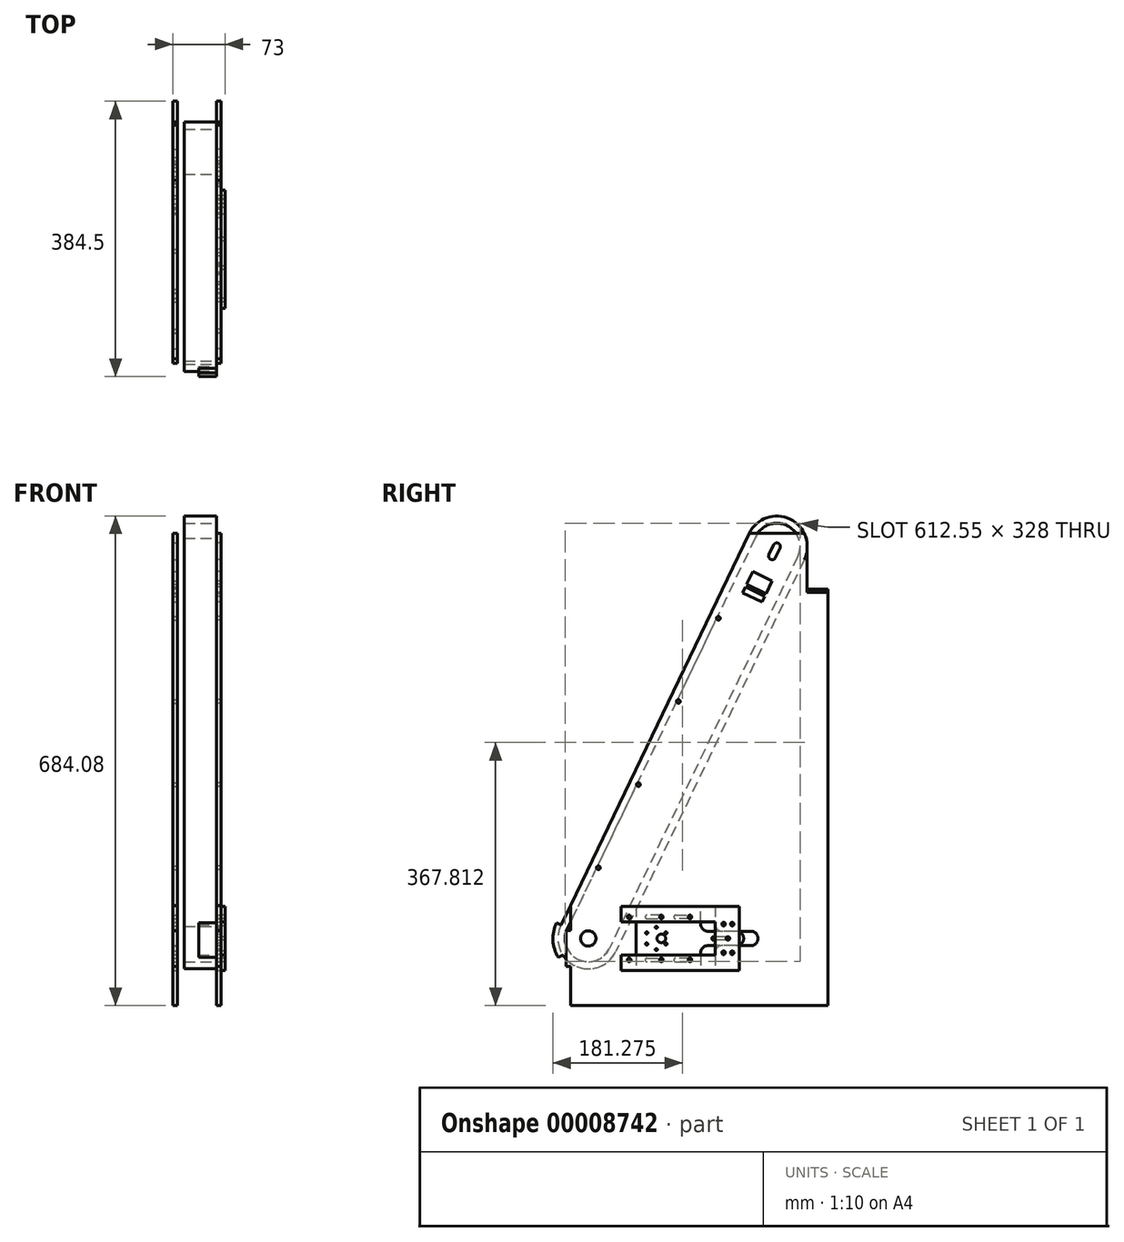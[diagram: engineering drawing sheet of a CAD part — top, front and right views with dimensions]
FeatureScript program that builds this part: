
annotation { "Feature Type Name" : "Feature", "Feature Type Description" : "" }
export const myFeature = defineFeature(function(context is Context, id is Id, definition is map)
    precondition{}
    {
        {
            var Q0;
            Q0=qCreatedBy(makeId("Right.planeOp"),FACE);
            var sketch = newSketch(context, id + "F0", { "sketchPlane" : qUnion([Q0])});
            skLineSegment(sketch, "E0", {"start": v(-250, 0) * mm, "end": v(-250, 45) * mm});
            skLineSegment(sketch, "E1", {"start": v(-250, 130) * mm, "end": v(0, 650) * mm});
            skLineSegment(sketch, "E2", {"start": v(0, 650) * mm, "end": v(0, 650) * mm});
            skLineSegment(sketch, "E3", {"start": v(0, 650) * mm, "end": v(0, 0) * mm, "construction": true});
            skLineSegment(sketch, "E4", {"start": v(0, 0) * mm, "end": v(-250, 0) * mm, "construction": true});
            skCircle(sketch, "E5", {"center": v(-225, 83.91) * mm, "radius": 32.5 * mm, "construction": true});
            skCircle(sketch, "E6", {"center": v(38.3, 631.58) * mm, "radius": 32.5 * mm, "construction": true});
            skLineSegment(sketch, "E7.bottom", {"start": v(-250, 0) * mm, "end": v(-400, 0) * mm, "construction": true});
            skLineSegment(sketch, "E7.top", {"start": v(-250, 130) * mm, "end": v(-400, 130) * mm, "construction": true});
            skLineSegment(sketch, "E7.left", {"start": v(-250, 0) * mm, "end": v(-250, 130) * mm, "construction": true});
            skLineSegment(sketch, "E7.right", {"start": v(-400, 0) * mm, "end": v(-400, 130) * mm, "construction": true});
            skLineSegment(sketch, "E8.bottom", {"start": v(0, 650) * mm, "end": v(150, 650) * mm, "construction": true});
            skLineSegment(sketch, "E8.top", {"start": v(0, 0) * mm, "end": v(150, 0) * mm, "construction": true});
            skLineSegment(sketch, "E8.right", {"start": v(150, 650) * mm, "end": v(150, 0) * mm, "construction": true});
            skLineSegment(sketch, "E9", {"start": v(110, 567.38) * mm, "end": v(110, 0) * mm});
            skCircle(sketch, "E10", {"center": v(38.3, 631.58) * mm, "radius": 42.5 * mm, "construction": true});
            skLineSegment(sketch, "E11", {"start": v(-215, 0) * mm, "end": v(-215, 122.02) * mm, "construction": true});
            skLineSegment(sketch, "E12", {"start": v(-215, 122.02) * mm, "end": v(-250, 130) * mm, "construction": true});
            skLineSegment(sketch, "E13", {"start": v(-215, 122.02) * mm, "end": v(-35, 496.42) * mm, "construction": true});
            skLineSegment(sketch, "E14", {"start": v(-35, 577.2) * mm, "end": v(-35, 0) * mm, "construction": true});
            skLineSegment(sketch, "E15.bottom", {"start": v(-250, 130) * mm, "end": v(-256, 130) * mm, "construction": true});
            skLineSegment(sketch, "E15.top", {"start": v(-250, 0) * mm, "end": v(-256, 0) * mm, "construction": true});
            skLineSegment(sketch, "E15.left", {"start": v(-250, 130) * mm, "end": v(-250, 0) * mm, "construction": true});
            skLineSegment(sketch, "E15.right", {"start": v(-256, 130) * mm, "end": v(-256, 0) * mm, "construction": true});
            skLineSegment(sketch, "E16.bottom", {"start": v(-256, 0) * mm, "end": v(-262, 0) * mm, "construction": true});
            skLineSegment(sketch, "E16.top", {"start": v(-256, 130) * mm, "end": v(-262, 130) * mm, "construction": true});
            skLineSegment(sketch, "E16.left", {"start": v(-256, 0) * mm, "end": v(-256, 130) * mm, "construction": true});
            skLineSegment(sketch, "E16.right", {"start": v(-262, 0) * mm, "end": v(-262, 130) * mm, "construction": true});
            skLineSegment(sketch, "E17.bottom", {"start": v(-215, 0) * mm, "end": v(-35, 0) * mm, "construction": true});
            skLineSegment(sketch, "E17.top", {"start": v(-215, 35) * mm, "end": v(-35, 35) * mm, "construction": true});
            skLineSegment(sketch, "E17.left", {"start": v(-215, 0) * mm, "end": v(-215, 35) * mm, "construction": true});
            skLineSegment(sketch, "E17.right", {"start": v(-35, 0) * mm, "end": v(-35, 35) * mm, "construction": true});
            skLineSegment(sketch, "E18.bottom", {"start": v(-215, 122.02) * mm, "end": v(-35, 122.02) * mm, "construction": true});
            skLineSegment(sketch, "E18.top", {"start": v(-215, 83.91) * mm, "end": v(-35, 83.91) * mm, "construction": true});
            skLineSegment(sketch, "E18.left", {"start": v(-215, 122.02) * mm, "end": v(-215, 83.91) * mm, "construction": true});
            skLineSegment(sketch, "E19", {"start": v(76.6, 650) * mm, "end": v(0, 650) * mm});
            skLineSegment(sketch, "E20", {"start": v(110, 0) * mm, "end": v(-35, 0) * mm, "construction": true});
            skArc(sketch, "E21", {"start": v(42.8, 629.42) * mm, "mid": v(40.47, 636.1) * mm, "end": v(33.8, 633.75) * mm});
            skLineSegment(sketch, "E22", {"start": v(33.8, 633.75) * mm, "end": v(27.3, 620.23) * mm});
            skLineSegment(sketch, "E23", {"start": v(42.8, 629.42) * mm, "end": v(36.31, 615.9) * mm});
            skArc(sketch, "E24.trimOffspring", {"start": v(27.3, 620.23) * mm, "mid": v(29.64, 613.56) * mm, "end": v(36.31, 615.9) * mm});
            skArc(sketch, "E25", {"start": v(80.8, 631.58) * mm, "mid": v(79.74, 641.03) * mm, "end": v(76.6, 650) * mm});
            skLineSegment(sketch, "E26", {"start": v(80.8, 631.58) * mm, "end": v(80.8, 567.38) * mm});
            skLineSegment(sketch, "E27", {"start": v(80.8, 567.38) * mm, "end": v(110, 567.38) * mm});
            skLineSegment(sketch, "E28.bottom", {"start": v(-5.55, 575) * mm, "end": v(21.5, 562) * mm});
            skLineSegment(sketch, "E28.top", {"start": v(-9.45, 566.89) * mm, "end": v(17.6, 553.89) * mm});
            skLineSegment(sketch, "E28.left", {"start": v(-5.55, 575) * mm, "end": v(-9.45, 566.89) * mm});
            skLineSegment(sketch, "E28.right", {"start": v(21.5, 562) * mm, "end": v(17.6, 553.89) * mm});
            skCircle(sketch, "E29", {"center": v(-43.2, 531.3) * mm, "radius": 2.5 * mm});
            skCircle(sketch, "E30", {"center": v(-154.93, 298.9) * mm, "radius": 2.5 * mm});
            skCircle(sketch, "E31", {"center": v(-210.8, 182.7) * mm, "radius": 2.5 * mm});
            skCircle(sketch, "E32", {"center": v(-99.06, 415.1) * mm, "radius": 2.5 * mm});
            skLineSegment(sketch, "E33", {"start": v(-43.2, 531.3) * mm, "end": v(-99.06, 415.1) * mm, "construction": true});
            skLineSegment(sketch, "E34", {"start": v(-99.06, 415.1) * mm, "end": v(-154.93, 298.9) * mm, "construction": true});
            skLineSegment(sketch, "E35", {"start": v(-154.93, 298.9) * mm, "end": v(-210.8, 182.7) * mm, "construction": true});
            skLineSegment(sketch, "E36.trimOffspring", {"start": v(-250, 95) * mm, "end": v(-250, 130) * mm});
            skLineSegment(sketch, "E37", {"start": v(-250, 45) * mm, "end": v(-256, 45) * mm});
            skLineSegment(sketch, "E38", {"start": v(-256, 45) * mm, "end": v(-256, 95) * mm});
            skLineSegment(sketch, "E39", {"start": v(-250, 95) * mm, "end": v(-256, 95) * mm});
            skCircle(sketch, "E40", {"center": v(-225, 83.91) * mm, "radius": 42.5 * mm, "construction": true});
            skCircle(sketch, "E41", {"center": v(-225, 83.91) * mm, "radius": 10.75 * mm});
            skLineSegment(sketch, "E42", {"start": v(38.3, 631.58) * mm, "end": v(-225, 83.91) * mm, "construction": true});
            skLineSegment(sketch, "E43", {"start": v(7.97, 568.5) * mm, "end": v(4.07, 560.39) * mm, "construction": true});
            skArc(sketch, "E44", {"start": v(-103, 77.41) * mm, "mid": v(-96.5, 83.91) * mm, "end": v(-103, 90.41) * mm, "construction": true});
            skArc(sketch, "E45", {"start": v(-123, 90.41) * mm, "mid": v(-129.5, 83.91) * mm, "end": v(-123, 77.41) * mm, "construction": true});
            skLineSegment(sketch, "E46", {"start": v(-123, 90.41) * mm, "end": v(-103, 90.41) * mm, "construction": true});
            skLineSegment(sketch, "E47", {"start": v(-103, 77.41) * mm, "end": v(-123, 77.41) * mm, "construction": true});
            skArc(sketch, "E48", {"start": v(-143, 116.41) * mm, "mid": v(-145.5, 113.91) * mm, "end": v(-143, 111.41) * mm, "construction": true});
            skArc(sketch, "E49", {"start": v(-123, 111.41) * mm, "mid": v(-120.5, 113.91) * mm, "end": v(-123, 116.41) * mm, "construction": true});
            skLineSegment(sketch, "E50", {"start": v(-123, 116.41) * mm, "end": v(-143, 116.41) * mm, "construction": true});
            skLineSegment(sketch, "E51", {"start": v(-143, 111.41) * mm, "end": v(-123, 111.41) * mm, "construction": true});
            skLineSegment(sketch, "E52", {"start": v(-113, 90.41) * mm, "end": v(-113, 77.41) * mm, "construction": true});
            skLineSegment(sketch, "E53.0.MirrorCS", {"start": v(-83, 111.41) * mm, "end": v(-103, 111.41) * mm, "construction": true});
            skArc(sketch, "E54.0.MirrorCS", {"start": v(-103, 111.41) * mm, "mid": v(-105.5, 113.91) * mm, "end": v(-103, 116.41) * mm, "construction": true});
            skLineSegment(sketch, "E55.0.MirrorCS", {"start": v(-103, 116.41) * mm, "end": v(-83, 116.41) * mm, "construction": true});
            skArc(sketch, "E56.0.MirrorCS", {"start": v(-83, 116.41) * mm, "mid": v(-80.5, 113.91) * mm, "end": v(-83, 111.41) * mm, "construction": true});
            skLineSegment(sketch, "E57.0.MirrorCS", {"start": v(-123, 51.41) * mm, "end": v(-143, 51.41) * mm, "construction": true});
            skArc(sketch, "E58.0.MirrorCS", {"start": v(-143, 51.41) * mm, "mid": v(-145.5, 53.91) * mm, "end": v(-143, 56.41) * mm, "construction": true});
            skLineSegment(sketch, "E59.0.MirrorCS", {"start": v(-103, 51.41) * mm, "end": v(-83, 51.41) * mm, "construction": true});
            skArc(sketch, "E60.0.MirrorCS", {"start": v(-123, 56.41) * mm, "mid": v(-120.5, 53.91) * mm, "end": v(-123, 51.41) * mm, "construction": true});
            skLineSegment(sketch, "E61.0.MirrorCS", {"start": v(-143, 56.41) * mm, "end": v(-123, 56.41) * mm, "construction": true});
            skArc(sketch, "E62.0.MirrorCS", {"start": v(-103, 56.41) * mm, "mid": v(-105.5, 53.91) * mm, "end": v(-103, 51.41) * mm, "construction": true});
            skLineSegment(sketch, "E63.0.MirrorCS", {"start": v(-83, 56.41) * mm, "end": v(-103, 56.41) * mm, "construction": true});
            skArc(sketch, "E64.0.MirrorCS", {"start": v(-83, 51.41) * mm, "mid": v(-80.5, 53.91) * mm, "end": v(-83, 56.41) * mm, "construction": true});
            skLineSegment(sketch, "E65", {"start": v(-250, 0) * mm, "end": v(-250, -10) * mm});
            skLineSegment(sketch, "E66", {"start": v(-250, -10) * mm, "end": v(110, -10) * mm});
            skLineSegment(sketch, "E67", {"start": v(110, -10) * mm, "end": v(110, 0) * mm});
            skLineSegment(sketch, "E68.bottom", {"start": v(-158, 128.91) * mm, "end": v(-48, 128.91) * mm});
            skLineSegment(sketch, "E68.top", {"start": v(-158, 38.91) * mm, "end": v(-48, 38.91) * mm});
            skLineSegment(sketch, "E68.left", {"start": v(-158, 128.91) * mm, "end": v(-158, 38.91) * mm});
            skLineSegment(sketch, "E68.right", {"start": v(-48, 128.91) * mm, "end": v(-48, 103.91) * mm});
            skLineSegment(sketch, "E69", {"start": v(2, 93.91) * mm, "end": v(-38, 93.91) * mm});
            skLineSegment(sketch, "E70", {"start": v(2, 73.91) * mm, "end": v(-38, 73.91) * mm});
            skLineSegment(sketch, "E71.trimOffspring", {"start": v(-48, 63.91) * mm, "end": v(-48, 38.91) * mm});
            skCircle(sketch, "E72", {"center": v(-36, 103.91) * mm, "radius": 2.5 * mm});
            skCircle(sketch, "E73", {"center": v(-24, 103.91) * mm, "radius": 2.5 * mm});
            skCircle(sketch, "E74.0.MirrorC", {"center": v(-36, 63.91) * mm, "radius": 2.5 * mm});
            skCircle(sketch, "E75.0.MirrorC", {"center": v(-24, 63.91) * mm, "radius": 2.5 * mm});
            skPoint(sketch, "E76.visualSharp", {"position": v(-48, 93.91) * mm});
            skArc(sketch, "E76.filletArc", {"start": v(-48, 103.91) * mm, "mid": v(-45.07, 96.84) * mm, "end": v(-38, 93.91) * mm});
            skPoint(sketch, "E77.visualSharp", {"position": v(-48, 73.91) * mm});
            skArc(sketch, "E77.filletArc", {"start": v(-38, 73.91) * mm, "mid": v(-45.07, 70.99) * mm, "end": v(-48, 63.91) * mm});
            skArc(sketch, "E78", {"start": v(2, 73.91) * mm, "mid": v(12, 83.91) * mm, "end": v(2, 93.91) * mm});
            skCircle(sketch, "E79", {"center": v(-168, 113.91) * mm, "radius": 2.5 * mm});
            skCircle(sketch, "E80", {"center": v(-168, 53.91) * mm, "radius": 2.5 * mm});
            skLineSegment(sketch, "E81", {"start": v(23.22, 565.6) * mm, "end": v(-3.81, 578.6) * mm});
            skLineSegment(sketch, "E82", {"start": v(-3.81, 578.6) * mm, "end": v(4.85, 596.63) * mm});
            skLineSegment(sketch, "E83", {"start": v(4.85, 596.63) * mm, "end": v(31.9, 583.63) * mm});
            skLineSegment(sketch, "E84", {"start": v(31.9, 583.63) * mm, "end": v(23.22, 565.6) * mm});
            skSolve(sketch);
        }
        {
            var Q0;
            Q0 = qSketchRegion(id + "F0", true);
            extrude(context, id + "F1", {"entities" : qUnion([Q0]), "depth" : 6 * mm});
        }
        {
            var Q0;
            Q0=makeQuery(id+"F0.imprint","IMPRINT",FACE,{"disambiguationData":[TD([[makeQuery(id+"F0.imprint","IMPRINT",EDGE,{"derivedFrom":sQuery(id+"F0.wireOp",EDGE,"E0")}),-1.0]])]});
            var sketch = newSketch(context, id + "F2", { "sketchPlane" : qUnion([Q0])});
            skArc(sketch, "E85.0", {"start": v(-263.3, 102.33) * mm, "mid": v(-243.42, 45.61) * mm, "end": v(-186.7, 65.5) * mm});
            skLineSegment(sketch, "E85.1", {"start": v(76.63, 613.22) * mm, "end": v(-186.7, 65.5) * mm});
            skLineSegment(sketch, "E85.2", {"start": v(67.61, 617.55) * mm, "end": v(-195.7, 69.83) * mm});
            skArc(sketch, "E85.3", {"start": v(-252.97, 100.46) * mm, "mid": v(-240.33, 55.26) * mm, "end": v(-195.7, 69.83) * mm});
            skLineSegment(sketch, "E85.4", {"start": v(-250, 130) * mm, "end": v(0, 650) * mm});
            skArc(sketch, "E85.5", {"start": v(76.63, 613.22) * mm, "mid": v(56.7, 669.9) * mm, "end": v(0, 650) * mm});
            skArc(sketch, "E85.6", {"start": v(67.61, 617.55) * mm, "mid": v(51.09, 661.46) * mm, "end": v(7.9, 643.1) * mm});
            skLineSegment(sketch, "E86", {"start": v(7.9, 643.1) * mm, "end": v(-252.97, 100.46) * mm});
            skLineSegment(sketch, "E87", {"start": v(-250, 130) * mm, "end": v(-263.3, 102.33) * mm});
            skSolve(sketch);
        }
        {
            var Q0;
            Q0 = qSketchRegion(id + "F2", true);
            extrude(context, id + "F3", {"entities" : qUnion([Q0]), "oppositeDirection" : true, "depth" : 45 * mm});
        }
        {
            var Q0;
            Q0=makeQuery(id+"F3.opExtrude","CAP_FACE",FACE,{"disambiguationData":[OSD([sQuery(id+"F2.wireOp",EDGE,"E85.0"),sQuery(id+"F2.wireOp",EDGE,"E85.1"),sQuery(id+"F2.wireOp",EDGE,"E85.2"),sQuery(id+"F2.wireOp",EDGE,"E85.3"),sQuery(id+"F2.wireOp",EDGE,"E85.4"),sQuery(id+"F2.wireOp",EDGE,"E85.5"),sQuery(id+"F2.wireOp",EDGE,"E85.6"),sQuery(id+"F2.wireOp",EDGE,"E86"),sQuery(id+"F2.wireOp",EDGE,"E87")])],"isStart":true});
            var sketch = newSketch(context, id + "F4", { "sketchPlane" : qUnion([Q0])});
            skArc(sketch, "E88", {"start": v(-269.4, 105.8) * mm, "mid": v(-274.43, 81.35) * mm, "end": v(-266.9, 57.55) * mm});
            skLineSegment(sketch, "E89", {"start": v(-269.4, 105.8) * mm, "end": v(-263.3, 102.33) * mm});
            skLineSegment(sketch, "E90", {"start": v(-266.9, 57.55) * mm, "end": v(-260.81, 61.03) * mm});
            skArc(sketch, "E91", {"start": v(-263.3, 102.33) * mm, "mid": v(-267.42, 81.36) * mm, "end": v(-260.81, 61.03) * mm});
            skSolve(sketch);
        }
        {
            var Q0;
            Q0 = qSketchRegion(id + "F4", true);
            extrude(context, id + "F5", {"entities" : qUnion([Q0]), "operationType" : NewBodyOperationType.ADD, "oppositeDirection" : true, "depth" : 25 * mm});
        }
        {
            var Q0;
            Q0=makeQuery(id+"F1.opExtrude","CAP_FACE",FACE,{"disambiguationData":[OSD([sQuery(id+"F0.wireOp",EDGE,"E0"),sQuery(id+"F0.wireOp",EDGE,"E1"),sQuery(id+"F0.wireOp",EDGE,"E9"),sQuery(id+"F0.wireOp",EDGE,"E19"),sQuery(id+"F0.wireOp",EDGE,"E21"),sQuery(id+"F0.wireOp",EDGE,"E22"),sQuery(id+"F0.wireOp",EDGE,"E23"),sQuery(id+"F0.wireOp",EDGE,"E24.trimOffspring"),sQuery(id+"F0.wireOp",EDGE,"E25"),sQuery(id+"F0.wireOp",EDGE,"E26"),sQuery(id+"F0.wireOp",EDGE,"E27"),sQuery(id+"F0.wireOp",EDGE,"E28.bottom"),sQuery(id+"F0.wireOp",EDGE,"E28.top"),sQuery(id+"F0.wireOp",EDGE,"E28.left"),sQuery(id+"F0.wireOp",EDGE,"E28.right"),sQuery(id+"F0.wireOp",EDGE,"E29"),sQuery(id+"F0.wireOp",EDGE,"E30"),sQuery(id+"F0.wireOp",EDGE,"E31"),sQuery(id+"F0.wireOp",EDGE,"E32"),sQuery(id+"F0.wireOp",EDGE,"E36.trimOffspring"),sQuery(id+"F0.wireOp",EDGE,"E37"),sQuery(id+"F0.wireOp",EDGE,"E38"),sQuery(id+"F0.wireOp",EDGE,"E39"),sQuery(id+"F0.wireOp",EDGE,"E41"),sQuery(id+"F0.wireOp",EDGE,"E65"),sQuery(id+"F0.wireOp",EDGE,"E66"),sQuery(id+"F0.wireOp",EDGE,"E67"),sQuery(id+"F0.wireOp",EDGE,"E68.bottom"),sQuery(id+"F0.wireOp",EDGE,"E68.top"),sQuery(id+"F0.wireOp",EDGE,"E68.left"),sQuery(id+"F0.wireOp",EDGE,"E68.right"),sQuery(id+"F0.wireOp",EDGE,"E69"),sQuery(id+"F0.wireOp",EDGE,"E70"),sQuery(id+"F0.wireOp",EDGE,"E71.trimOffspring"),sQuery(id+"F0.wireOp",EDGE,"E72"),sQuery(id+"F0.wireOp",EDGE,"E73"),sQuery(id+"F0.wireOp",EDGE,"E74.0.MirrorC"),sQuery(id+"F0.wireOp",EDGE,"E75.0.MirrorC"),sQuery(id+"F0.wireOp",EDGE,"E76.filletArc"),sQuery(id+"F0.wireOp",EDGE,"E77.filletArc"),sQuery(id+"F0.wireOp",EDGE,"E78"),sQuery(id+"F0.wireOp",EDGE,"5232d4b0-3cc3-4d14-9a51-cdb3d410511d.0.MirrorCS"),sQuery(id+"F0.wireOp",EDGE,"e2d33160-89aa-41c8-a270-ced146764406.0.MirrorCS"),sQuery(id+"F0.wireOp",EDGE,"e187159f-ad14-482b-9280-8cc7652cb730.0.MirrorCS"),sQuery(id+"F0.wireOp",EDGE,"d5b84b43-e90d-4140-bfef-c8227e2ab3ce.0.MirrorCS"),sQuery(id+"F0.wireOp",EDGE,"901432f0-0f95-4989-9cc0-a0deb5664f3d.0.MirrorCS"),sQuery(id+"F0.wireOp",EDGE,"20d51c83-01ba-4d90-888a-5c5246788dde.0.MirrorCS"),sQuery(id+"F0.wireOp",EDGE,"919df3ca-f2c8-442f-8c62-a2348701ab05.0.MirrorCS"),sQuery(id+"F0.wireOp",EDGE,"f4d91b0f-c379-4811-a7c1-4052a48fdef3.0.MirrorCS"),sQuery(id+"F0.wireOp",EDGE,"65e59967-7406-4aeb-97f1-becdd296b569.0.MirrorCS"),sQuery(id+"F0.wireOp",EDGE,"80b0b28f-4663-4f58-9bb3-9a96ce068a37.0.MirrorCS"),sQuery(id+"F0.wireOp",EDGE,"c9f270f5-1f51-4d0d-ae3f-d0e4d7b2f217.0.MirrorCS"),sQuery(id+"F0.wireOp",EDGE,"a8867294-c913-42ce-a77f-fa8c65982e2f.0.MirrorCS"),sQuery(id+"F0.wireOp",EDGE,"a8dd77a0-3a93-456d-83c1-19a94e0bbaab.0.MirrorCS"),sQuery(id+"F0.wireOp",EDGE,"77da776a-dfef-4cf4-8eb2-1489e33f5686.0.MirrorCS"),sQuery(id+"F0.wireOp",EDGE,"566fd665-dcc4-43ef-a258-170fd602a317.0.MirrorCS"),sQuery(id+"F0.wireOp",EDGE,"d3467c6b-eefe-44c7-bab6-9067eb3a1ad1.0.MirrorCS")])],"isStart":false});
            var sketch = newSketch(context, id + "F6", { "sketchPlane" : qUnion([Q0])});
            skLineSegment(sketch, "E92.bottom", {"start": v(-158, 128.91) * mm, "end": v(-68, 128.91) * mm});
            skLineSegment(sketch, "E92.top", {"start": v(-158, 38.91) * mm, "end": v(-68, 38.91) * mm});
            skLineSegment(sketch, "E92.left", {"start": v(-158, 128.91) * mm, "end": v(-158, 38.91) * mm});
            skCircle(sketch, "E93", {"center": v(-123, 83.91) * mm, "radius": 6 * mm});
            skArc(sketch, "E94", {"start": v(-18, 73.91) * mm, "mid": v(-8, 83.91) * mm, "end": v(-18, 93.91) * mm});
            skLineSegment(sketch, "E95", {"start": v(-18, 73.91) * mm, "end": v(-58, 73.91) * mm});
            skLineSegment(sketch, "E96", {"start": v(-68, 63.91) * mm, "end": v(-68, 38.91) * mm});
            skLineSegment(sketch, "E97", {"start": v(-18, 93.91) * mm, "end": v(-58, 93.91) * mm});
            skLineSegment(sketch, "E98", {"start": v(-68, 103.91) * mm, "end": v(-68, 128.91) * mm});
            skArc(sketch, "E99", {"start": v(-30, 81.41) * mm, "mid": v(-27.5, 83.91) * mm, "end": v(-30, 86.41) * mm});
            skLineSegment(sketch, "E100", {"start": v(-30, 86.41) * mm, "end": v(-50, 86.41) * mm});
            skLineSegment(sketch, "E101", {"start": v(-30, 81.41) * mm, "end": v(-50, 81.41) * mm});
            skArc(sketch, "E102", {"start": v(-50, 86.41) * mm, "mid": v(-52.5, 83.91) * mm, "end": v(-50, 81.41) * mm});
            skPoint(sketch, "E103.visualSharp", {"position": v(-68, 93.91) * mm});
            skArc(sketch, "E103.filletArc", {"start": v(-68, 103.91) * mm, "mid": v(-65.07, 96.84) * mm, "end": v(-58, 93.91) * mm});
            skPoint(sketch, "E104.visualSharp", {"position": v(-68, 73.91) * mm});
            skArc(sketch, "E104.filletArc", {"start": v(-58, 73.91) * mm, "mid": v(-65.07, 70.99) * mm, "end": v(-68, 63.91) * mm});
            skLineSegment(sketch, "E105", {"start": v(-8, 83.91) * mm, "end": v(12, 83.91) * mm, "construction": true});
            skLineSegment(sketch, "E106", {"start": v(-36, 103.91) * mm, "end": v(-24, 103.91) * mm, "construction": true});
            skLineSegment(sketch, "E107", {"start": v(-30, 103.91) * mm, "end": v(-30, 63.91) * mm, "construction": true});
            skLineSegment(sketch, "E108", {"start": v(-24, 63.91) * mm, "end": v(-36, 63.91) * mm, "construction": true});
            skCircle(sketch, "E109", {"center": v(-130, 83.91) * mm, "radius": 15.5 * mm, "construction": true});
            skCircle(sketch, "E110", {"center": v(-143.42, 91.66) * mm, "radius": 1.5 * mm});
            skCircle(sketch, "E111", {"center": v(-143.42, 76.16) * mm, "radius": 1.5 * mm});
            skCircle(sketch, "E112", {"center": v(-130, 68.41) * mm, "radius": 1.5 * mm});
            skCircle(sketch, "E113", {"center": v(-130, 99.41) * mm, "radius": 1.5 * mm});
            skCircle(sketch, "E114", {"center": v(-116.58, 91.66) * mm, "radius": 1.5 * mm});
            skLineSegment(sketch, "E115.2", {"start": v(-215, 83.91) * mm, "end": v(-35, 83.91) * mm});
            skLineSegment(sketch, "E116", {"start": v(-130, 83.91) * mm, "end": v(-130, 99.41) * mm, "construction": true});
            skLineSegment(sketch, "E117", {"start": v(-130, 83.91) * mm, "end": v(-143.42, 76.16) * mm, "construction": true});
            skLineSegment(sketch, "E118", {"start": v(-130, 83.91) * mm, "end": v(-116.58, 91.66) * mm, "construction": true});
            skLineSegment(sketch, "E119", {"start": v(-130, 83.91) * mm, "end": v(-130, 68.41) * mm, "construction": true});
            skCircle(sketch, "E120", {"center": v(-116.58, 76.16) * mm, "radius": 1.5 * mm});
            skLineSegment(sketch, "E121", {"start": v(-130, 83.91) * mm, "end": v(-143.42, 91.66) * mm, "construction": true});
            skLineSegment(sketch, "E122", {"start": v(-130, 83.91) * mm, "end": v(-116.58, 76.16) * mm, "construction": true});
            skLineSegment(sketch, "E123.0", {"start": v(-123, 116.41) * mm, "end": v(-143, 116.41) * mm});
            skArc(sketch, "E123.1", {"start": v(-123, 111.41) * mm, "mid": v(-120.5, 113.91) * mm, "end": v(-123, 116.41) * mm});
            skLineSegment(sketch, "E123.2", {"start": v(-103, 116.41) * mm, "end": v(-83, 116.41) * mm});
            skArc(sketch, "E123.3", {"start": v(-103, 111.41) * mm, "mid": v(-105.5, 113.91) * mm, "end": v(-103, 116.41) * mm});
            skLineSegment(sketch, "E123.4", {"start": v(-83, 111.41) * mm, "end": v(-103, 111.41) * mm});
            skArc(sketch, "E123.5", {"start": v(-83, 116.41) * mm, "mid": v(-80.5, 113.91) * mm, "end": v(-83, 111.41) * mm});
            skLineSegment(sketch, "E123.6", {"start": v(-143, 111.41) * mm, "end": v(-123, 111.41) * mm});
            skArc(sketch, "E123.7", {"start": v(-143, 116.41) * mm, "mid": v(-145.5, 113.91) * mm, "end": v(-143, 111.41) * mm});
            skLineSegment(sketch, "E123.8", {"start": v(-143, 56.41) * mm, "end": v(-123, 56.41) * mm});
            skArc(sketch, "E123.9", {"start": v(-143, 51.41) * mm, "mid": v(-145.5, 53.91) * mm, "end": v(-143, 56.41) * mm});
            skLineSegment(sketch, "E123.10", {"start": v(-123, 51.41) * mm, "end": v(-143, 51.41) * mm});
            skArc(sketch, "E123.11", {"start": v(-123, 56.41) * mm, "mid": v(-120.5, 53.91) * mm, "end": v(-123, 51.41) * mm});
            skLineSegment(sketch, "E123.12", {"start": v(-83, 56.41) * mm, "end": v(-103, 56.41) * mm});
            skArc(sketch, "E123.13", {"start": v(-103, 56.41) * mm, "mid": v(-105.5, 53.91) * mm, "end": v(-103, 51.41) * mm});
            skLineSegment(sketch, "E123.14", {"start": v(-103, 51.41) * mm, "end": v(-83, 51.41) * mm});
            skArc(sketch, "E123.15", {"start": v(-83, 51.41) * mm, "mid": v(-80.5, 53.91) * mm, "end": v(-83, 56.41) * mm});
            skSolve(sketch);
        }
        {
            var Q0;
            Q0 = qSketchRegion(id + "F6", true);
            extrude(context, id + "F7", {"entities" : qUnion([Q0]), "oppositeDirection" : true, "depth" : 6 * mm});
        }
        {
            var Q0;
            Q0=makeQuery(id+"F1.opExtrude","CAP_FACE",FACE,{"disambiguationData":[OSD([sQuery(id+"F0.wireOp",EDGE,"E0"),sQuery(id+"F0.wireOp",EDGE,"E1"),sQuery(id+"F0.wireOp",EDGE,"E9"),sQuery(id+"F0.wireOp",EDGE,"E19"),sQuery(id+"F0.wireOp",EDGE,"E21"),sQuery(id+"F0.wireOp",EDGE,"E22"),sQuery(id+"F0.wireOp",EDGE,"E23"),sQuery(id+"F0.wireOp",EDGE,"E24.trimOffspring"),sQuery(id+"F0.wireOp",EDGE,"E25"),sQuery(id+"F0.wireOp",EDGE,"E26"),sQuery(id+"F0.wireOp",EDGE,"E27"),sQuery(id+"F0.wireOp",EDGE,"E28.bottom"),sQuery(id+"F0.wireOp",EDGE,"E28.top"),sQuery(id+"F0.wireOp",EDGE,"E28.left"),sQuery(id+"F0.wireOp",EDGE,"E28.right"),sQuery(id+"F0.wireOp",EDGE,"E29"),sQuery(id+"F0.wireOp",EDGE,"E30"),sQuery(id+"F0.wireOp",EDGE,"E31"),sQuery(id+"F0.wireOp",EDGE,"E32"),sQuery(id+"F0.wireOp",EDGE,"E36.trimOffspring"),sQuery(id+"F0.wireOp",EDGE,"E37"),sQuery(id+"F0.wireOp",EDGE,"E38"),sQuery(id+"F0.wireOp",EDGE,"E39"),sQuery(id+"F0.wireOp",EDGE,"E41"),sQuery(id+"F0.wireOp",EDGE,"E65"),sQuery(id+"F0.wireOp",EDGE,"E66"),sQuery(id+"F0.wireOp",EDGE,"E67"),sQuery(id+"F0.wireOp",EDGE,"E68.bottom"),sQuery(id+"F0.wireOp",EDGE,"E68.top"),sQuery(id+"F0.wireOp",EDGE,"E68.left"),sQuery(id+"F0.wireOp",EDGE,"E68.right"),sQuery(id+"F0.wireOp",EDGE,"E69"),sQuery(id+"F0.wireOp",EDGE,"E70"),sQuery(id+"F0.wireOp",EDGE,"E71.trimOffspring"),sQuery(id+"F0.wireOp",EDGE,"E72"),sQuery(id+"F0.wireOp",EDGE,"E73"),sQuery(id+"F0.wireOp",EDGE,"E74.0.MirrorC"),sQuery(id+"F0.wireOp",EDGE,"E75.0.MirrorC"),sQuery(id+"F0.wireOp",EDGE,"E76.filletArc"),sQuery(id+"F0.wireOp",EDGE,"E77.filletArc"),sQuery(id+"F0.wireOp",EDGE,"E78"),sQuery(id+"F0.wireOp",EDGE,"5232d4b0-3cc3-4d14-9a51-cdb3d410511d.0.MirrorCS"),sQuery(id+"F0.wireOp",EDGE,"e2d33160-89aa-41c8-a270-ced146764406.0.MirrorCS"),sQuery(id+"F0.wireOp",EDGE,"e187159f-ad14-482b-9280-8cc7652cb730.0.MirrorCS"),sQuery(id+"F0.wireOp",EDGE,"d5b84b43-e90d-4140-bfef-c8227e2ab3ce.0.MirrorCS"),sQuery(id+"F0.wireOp",EDGE,"901432f0-0f95-4989-9cc0-a0deb5664f3d.0.MirrorCS"),sQuery(id+"F0.wireOp",EDGE,"20d51c83-01ba-4d90-888a-5c5246788dde.0.MirrorCS"),sQuery(id+"F0.wireOp",EDGE,"919df3ca-f2c8-442f-8c62-a2348701ab05.0.MirrorCS"),sQuery(id+"F0.wireOp",EDGE,"f4d91b0f-c379-4811-a7c1-4052a48fdef3.0.MirrorCS"),sQuery(id+"F0.wireOp",EDGE,"65e59967-7406-4aeb-97f1-becdd296b569.0.MirrorCS"),sQuery(id+"F0.wireOp",EDGE,"80b0b28f-4663-4f58-9bb3-9a96ce068a37.0.MirrorCS"),sQuery(id+"F0.wireOp",EDGE,"c9f270f5-1f51-4d0d-ae3f-d0e4d7b2f217.0.MirrorCS"),sQuery(id+"F0.wireOp",EDGE,"a8867294-c913-42ce-a77f-fa8c65982e2f.0.MirrorCS"),sQuery(id+"F0.wireOp",EDGE,"a8dd77a0-3a93-456d-83c1-19a94e0bbaab.0.MirrorCS"),sQuery(id+"F0.wireOp",EDGE,"77da776a-dfef-4cf4-8eb2-1489e33f5686.0.MirrorCS"),sQuery(id+"F0.wireOp",EDGE,"566fd665-dcc4-43ef-a258-170fd602a317.0.MirrorCS"),sQuery(id+"F0.wireOp",EDGE,"d3467c6b-eefe-44c7-bab6-9067eb3a1ad1.0.MirrorCS")])],"isStart":false});
            var sketch = newSketch(context, id + "F8", { "sketchPlane" : qUnion([Q0])});
            skLineSegment(sketch, "E124.bottom", {"start": v(-48, 106.91) * mm, "end": v(-179, 106.91) * mm});
            skLineSegment(sketch, "E124.top", {"start": v(-14, 128.91) * mm, "end": v(-179, 128.91) * mm});
            skLineSegment(sketch, "E124.right", {"start": v(-179, 106.91) * mm, "end": v(-179, 128.91) * mm});
            skLineSegment(sketch, "E125.right", {"start": v(-14, 38.91) * mm, "end": v(-14, 128.91) * mm});
            skLineSegment(sketch, "E126", {"start": v(-158, 83.91) * mm, "end": v(-14, 83.91) * mm, "construction": true});
            skLineSegment(sketch, "E127.0.MirrorCS", {"start": v(-179, 60.91) * mm, "end": v(-179, 38.91) * mm});
            skLineSegment(sketch, "E128.0.MirrorCS", {"start": v(-48, 60.91) * mm, "end": v(-179, 60.91) * mm});
            skLineSegment(sketch, "E129.0.MirrorCS", {"start": v(-14, 38.91) * mm, "end": v(-179, 38.91) * mm});
            skCircle(sketch, "E130", {"center": v(-123, 113.91) * mm, "radius": 2.5 * mm});
            skCircle(sketch, "E131", {"center": v(-83, 113.91) * mm, "radius": 2.5 * mm});
            skCircle(sketch, "E132", {"center": v(-123, 53.91) * mm, "radius": 2.5 * mm});
            skCircle(sketch, "E133", {"center": v(-83, 53.91) * mm, "radius": 2.5 * mm});
            skCircle(sketch, "E134", {"center": v(-24, 103.91) * mm, "radius": 2.5 * mm});
            skCircle(sketch, "E135", {"center": v(-36, 103.91) * mm, "radius": 2.5 * mm});
            skCircle(sketch, "E136", {"center": v(-36, 63.91) * mm, "radius": 2.5 * mm});
            skCircle(sketch, "E137", {"center": v(-24, 63.91) * mm, "radius": 2.5 * mm});
            skLineSegment(sketch, "E138", {"start": v(-30, 111.91) * mm, "end": v(-30, 55.91) * mm, "construction": true});
            skLineSegment(sketch, "E139", {"start": v(-36, 103.91) * mm, "end": v(-30, 103.91) * mm, "construction": true});
            skLineSegment(sketch, "E140", {"start": v(-30, 103.91) * mm, "end": v(-24, 103.91) * mm, "construction": true});
            skCircle(sketch, "E141", {"center": v(-30, 83.91) * mm, "radius": 2.5 * mm});
            skLineSegment(sketch, "E142", {"start": v(-48, 60.91) * mm, "end": v(-48, 106.91) * mm});
            skCircle(sketch, "E143.0", {"center": v(-168, 113.91) * mm, "radius": 2.5 * mm});
            skCircle(sketch, "E143.1", {"center": v(-168, 53.91) * mm, "radius": 2.5 * mm});
            skSolve(sketch);
        }
        {
            var Q0;
            Q0 = qSketchRegion(id + "F8", true);
            extrude(context, id + "F9", {"entities" : qUnion([Q0]), "depth" : 6 * mm});
        }
        {
            var Q0;
            Q0=makeQuery(id+"F1.opExtrude","CAP_FACE",FACE,{"disambiguationData":[OSD([sQuery(id+"F0.wireOp",EDGE,"E0"),sQuery(id+"F0.wireOp",EDGE,"E1"),sQuery(id+"F0.wireOp",EDGE,"E9"),sQuery(id+"F0.wireOp",EDGE,"E19"),sQuery(id+"F0.wireOp",EDGE,"E21"),sQuery(id+"F0.wireOp",EDGE,"E22"),sQuery(id+"F0.wireOp",EDGE,"E23"),sQuery(id+"F0.wireOp",EDGE,"E24.trimOffspring"),sQuery(id+"F0.wireOp",EDGE,"E25"),sQuery(id+"F0.wireOp",EDGE,"E26"),sQuery(id+"F0.wireOp",EDGE,"E27"),sQuery(id+"F0.wireOp",EDGE,"E28.bottom"),sQuery(id+"F0.wireOp",EDGE,"E28.top"),sQuery(id+"F0.wireOp",EDGE,"E28.left"),sQuery(id+"F0.wireOp",EDGE,"E28.right"),sQuery(id+"F0.wireOp",EDGE,"E29"),sQuery(id+"F0.wireOp",EDGE,"E30"),sQuery(id+"F0.wireOp",EDGE,"E31"),sQuery(id+"F0.wireOp",EDGE,"E32"),sQuery(id+"F0.wireOp",EDGE,"E36.trimOffspring"),sQuery(id+"F0.wireOp",EDGE,"E37"),sQuery(id+"F0.wireOp",EDGE,"E38"),sQuery(id+"F0.wireOp",EDGE,"E39"),sQuery(id+"F0.wireOp",EDGE,"E41"),sQuery(id+"F0.wireOp",EDGE,"E65"),sQuery(id+"F0.wireOp",EDGE,"E66"),sQuery(id+"F0.wireOp",EDGE,"E67"),sQuery(id+"F0.wireOp",EDGE,"E68.bottom"),sQuery(id+"F0.wireOp",EDGE,"E68.top"),sQuery(id+"F0.wireOp",EDGE,"E68.left"),sQuery(id+"F0.wireOp",EDGE,"E68.right"),sQuery(id+"F0.wireOp",EDGE,"E69"),sQuery(id+"F0.wireOp",EDGE,"E70"),sQuery(id+"F0.wireOp",EDGE,"E71.trimOffspring"),sQuery(id+"F0.wireOp",EDGE,"E72"),sQuery(id+"F0.wireOp",EDGE,"E73"),sQuery(id+"F0.wireOp",EDGE,"E74.0.MirrorC"),sQuery(id+"F0.wireOp",EDGE,"E75.0.MirrorC"),sQuery(id+"F0.wireOp",EDGE,"E76.filletArc"),sQuery(id+"F0.wireOp",EDGE,"E77.filletArc"),sQuery(id+"F0.wireOp",EDGE,"E78"),sQuery(id+"F0.wireOp",EDGE,"E79"),sQuery(id+"F0.wireOp",EDGE,"E80"),sQuery(id+"F0.wireOp",EDGE,"E81"),sQuery(id+"F0.wireOp",EDGE,"E82"),sQuery(id+"F0.wireOp",EDGE,"E83"),sQuery(id+"F0.wireOp",EDGE,"E84")])],"isStart":false});
            cPlane(context, id + "F10", {"entities" : qUnion([Q0]), "cplaneType" : CPlaneType.OFFSET, "offset" : (67 / 2) * mm, "oppositeDirection" : true, "width" : 150 * mm, "height" : 150 * mm});
        }
        {
            var Q0;
            Q0=makeQuery(id+"F1.opExtrude","SWEPT_BODY",BODY,{"disambiguationData":[OSD([sQuery(id+"F0.wireOp",EDGE,"E0"),sQuery(id+"F0.wireOp",EDGE,"E1"),sQuery(id+"F0.wireOp",EDGE,"E9"),sQuery(id+"F0.wireOp",EDGE,"E19"),sQuery(id+"F0.wireOp",EDGE,"E21"),sQuery(id+"F0.wireOp",EDGE,"E22"),sQuery(id+"F0.wireOp",EDGE,"E23"),sQuery(id+"F0.wireOp",EDGE,"E24.trimOffspring"),sQuery(id+"F0.wireOp",EDGE,"E25"),sQuery(id+"F0.wireOp",EDGE,"E26"),sQuery(id+"F0.wireOp",EDGE,"E27"),sQuery(id+"F0.wireOp",EDGE,"E28.bottom"),sQuery(id+"F0.wireOp",EDGE,"E28.top"),sQuery(id+"F0.wireOp",EDGE,"E28.left"),sQuery(id+"F0.wireOp",EDGE,"E28.right"),sQuery(id+"F0.wireOp",EDGE,"E29"),sQuery(id+"F0.wireOp",EDGE,"E30"),sQuery(id+"F0.wireOp",EDGE,"E31"),sQuery(id+"F0.wireOp",EDGE,"E32"),sQuery(id+"F0.wireOp",EDGE,"E36.trimOffspring"),sQuery(id+"F0.wireOp",EDGE,"E37"),sQuery(id+"F0.wireOp",EDGE,"E38"),sQuery(id+"F0.wireOp",EDGE,"E39"),sQuery(id+"F0.wireOp",EDGE,"E41"),sQuery(id+"F0.wireOp",EDGE,"E65"),sQuery(id+"F0.wireOp",EDGE,"E66"),sQuery(id+"F0.wireOp",EDGE,"E67"),sQuery(id+"F0.wireOp",EDGE,"E68.bottom"),sQuery(id+"F0.wireOp",EDGE,"E68.top"),sQuery(id+"F0.wireOp",EDGE,"E68.left"),sQuery(id+"F0.wireOp",EDGE,"E68.right"),sQuery(id+"F0.wireOp",EDGE,"E69"),sQuery(id+"F0.wireOp",EDGE,"E70"),sQuery(id+"F0.wireOp",EDGE,"E71.trimOffspring"),sQuery(id+"F0.wireOp",EDGE,"E72"),sQuery(id+"F0.wireOp",EDGE,"E73"),sQuery(id+"F0.wireOp",EDGE,"E74.0.MirrorC"),sQuery(id+"F0.wireOp",EDGE,"E75.0.MirrorC"),sQuery(id+"F0.wireOp",EDGE,"E76.filletArc"),sQuery(id+"F0.wireOp",EDGE,"E77.filletArc"),sQuery(id+"F0.wireOp",EDGE,"E78"),sQuery(id+"F0.wireOp",EDGE,"E79"),sQuery(id+"F0.wireOp",EDGE,"E80"),sQuery(id+"F0.wireOp",EDGE,"E81"),sQuery(id+"F0.wireOp",EDGE,"E82"),sQuery(id+"F0.wireOp",EDGE,"E83"),sQuery(id+"F0.wireOp",EDGE,"E84")])]});
            var Q1;
            Q1=qCreatedBy(id+"F10.planeOp",FACE);
            mirror(context, id + "F11", {"entities" : qUnion([Q0]), "mirrorPlane" : qUnion([Q1])});
        }
        {
            var Q0;
            Q0=makeQuery(id+"F11.opPattern","COPY",FACE,{"derivedFrom":makeQuery(id+"F1.opExtrude","CAP_FACE",FACE,{"disambiguationData":[OSD([sQuery(id+"F0.wireOp",EDGE,"E0"),sQuery(id+"F0.wireOp",EDGE,"E1"),sQuery(id+"F0.wireOp",EDGE,"E9"),sQuery(id+"F0.wireOp",EDGE,"E19"),sQuery(id+"F0.wireOp",EDGE,"E21"),sQuery(id+"F0.wireOp",EDGE,"E22"),sQuery(id+"F0.wireOp",EDGE,"E23"),sQuery(id+"F0.wireOp",EDGE,"E24.trimOffspring"),sQuery(id+"F0.wireOp",EDGE,"E25"),sQuery(id+"F0.wireOp",EDGE,"E26"),sQuery(id+"F0.wireOp",EDGE,"E27"),sQuery(id+"F0.wireOp",EDGE,"E28.bottom"),sQuery(id+"F0.wireOp",EDGE,"E28.top"),sQuery(id+"F0.wireOp",EDGE,"E28.left"),sQuery(id+"F0.wireOp",EDGE,"E28.right"),sQuery(id+"F0.wireOp",EDGE,"E29"),sQuery(id+"F0.wireOp",EDGE,"E30"),sQuery(id+"F0.wireOp",EDGE,"E31"),sQuery(id+"F0.wireOp",EDGE,"E32"),sQuery(id+"F0.wireOp",EDGE,"E36.trimOffspring"),sQuery(id+"F0.wireOp",EDGE,"E37"),sQuery(id+"F0.wireOp",EDGE,"E38"),sQuery(id+"F0.wireOp",EDGE,"E39"),sQuery(id+"F0.wireOp",EDGE,"E41"),sQuery(id+"F0.wireOp",EDGE,"E65"),sQuery(id+"F0.wireOp",EDGE,"E66"),sQuery(id+"F0.wireOp",EDGE,"E67"),sQuery(id+"F0.wireOp",EDGE,"E68.bottom"),sQuery(id+"F0.wireOp",EDGE,"E68.top"),sQuery(id+"F0.wireOp",EDGE,"E68.left"),sQuery(id+"F0.wireOp",EDGE,"E68.right"),sQuery(id+"F0.wireOp",EDGE,"E69"),sQuery(id+"F0.wireOp",EDGE,"E70"),sQuery(id+"F0.wireOp",EDGE,"E71.trimOffspring"),sQuery(id+"F0.wireOp",EDGE,"E72"),sQuery(id+"F0.wireOp",EDGE,"E73"),sQuery(id+"F0.wireOp",EDGE,"E74.0.MirrorC"),sQuery(id+"F0.wireOp",EDGE,"E75.0.MirrorC"),sQuery(id+"F0.wireOp",EDGE,"E76.filletArc"),sQuery(id+"F0.wireOp",EDGE,"E77.filletArc"),sQuery(id+"F0.wireOp",EDGE,"E78"),sQuery(id+"F0.wireOp",EDGE,"E79"),sQuery(id+"F0.wireOp",EDGE,"E80"),sQuery(id+"F0.wireOp",EDGE,"E81"),sQuery(id+"F0.wireOp",EDGE,"E82"),sQuery(id+"F0.wireOp",EDGE,"E83"),sQuery(id+"F0.wireOp",EDGE,"E84")])],"isStart":false}),"instanceName":"1"});
            var sketch = newSketch(context, id + "F12", { "sketchPlane" : qUnion([Q0])});
            skLineSegment(sketch, "E144.bottom", {"start": v(-80.8, 567.38) * mm, "end": v(-110, 567.38) * mm});
            skLineSegment(sketch, "E144.top", {"start": v(-80.8, 571.64) * mm, "end": v(-110, 571.64) * mm});
            skLineSegment(sketch, "E144.left", {"start": v(-80.8, 567.38) * mm, "end": v(-80.8, 571.64) * mm});
            skLineSegment(sketch, "E144.right", {"start": v(-110, 567.38) * mm, "end": v(-110, 571.64) * mm});
            skSolve(sketch);
        }
        {
            var Q0;
            Q0 = qSketchRegion(id + "F12", true);
            extrude(context, id + "F13", {"entities" : qUnion([Q0]), "operationType" : NewBodyOperationType.ADD, "oppositeDirection" : true, "depth" : 6 * mm});
        }
    });
